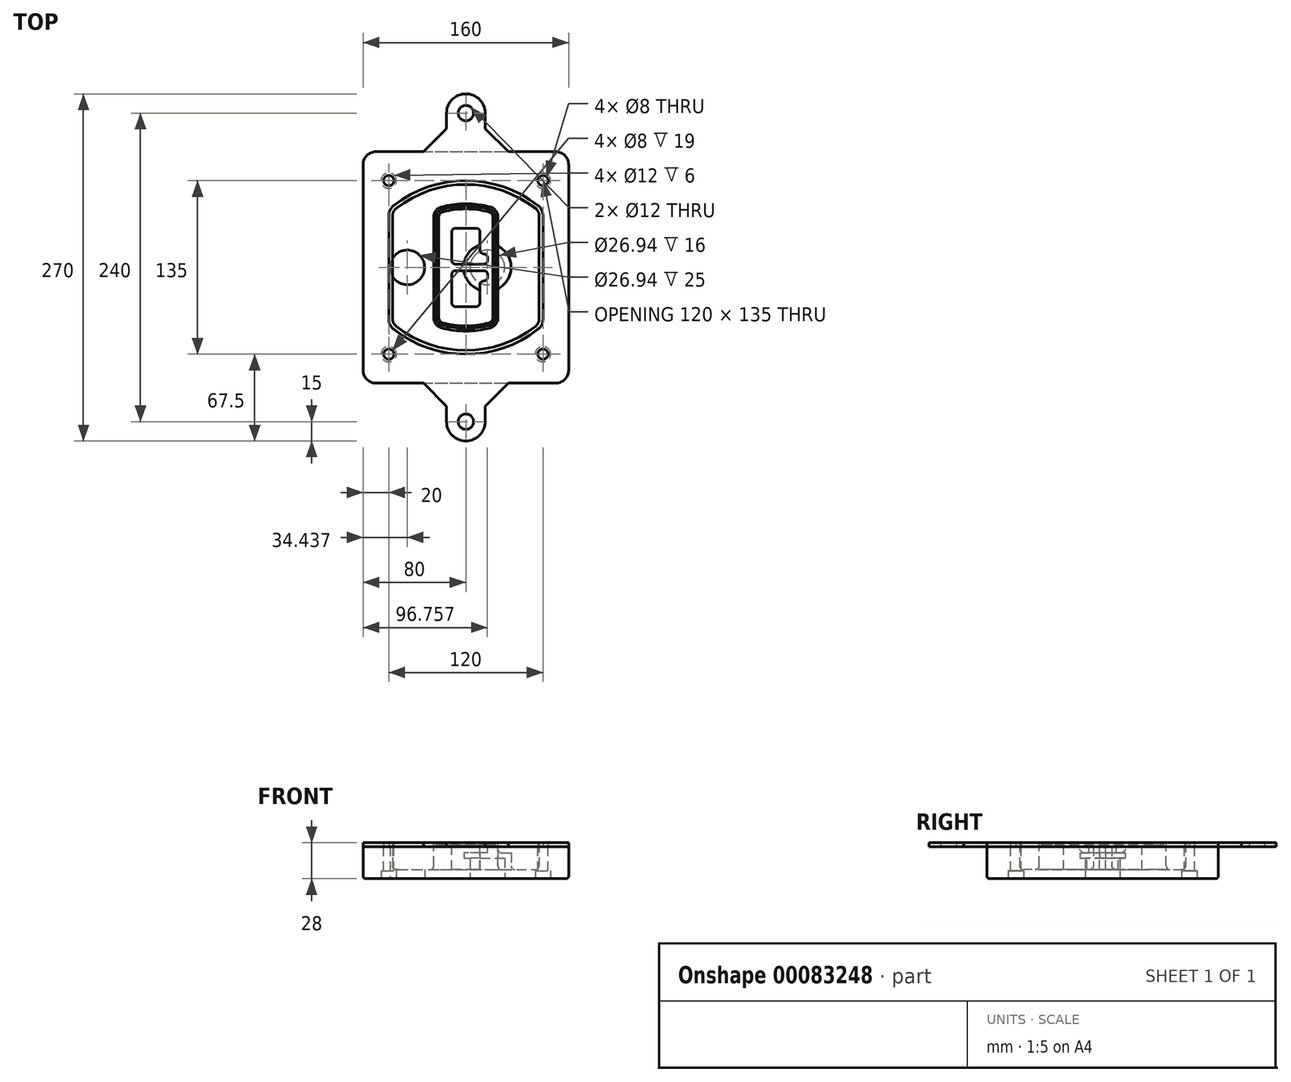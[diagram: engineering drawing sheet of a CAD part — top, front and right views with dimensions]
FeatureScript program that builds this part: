
annotation { "Feature Type Name" : "Feature", "Feature Type Description" : "" }
export const myFeature = defineFeature(function(context is Context, id is Id, definition is map)
    precondition{}
    {
        {
            var Q0;
            Q0=qCreatedBy(makeId("Top.planeOp"),FACE);
            var sketch = newSketch(context, id + "F0", { "sketchPlane" : qUnion([Q0])});
            skPoint(sketch, "E0.rect.middle", {"position": v(0, 0) * mm});
            skLineSegment(sketch, "E1.bottom", {"start": v(-70, -90) * mm, "end": v(70, -90) * mm});
            skLineSegment(sketch, "E1.top", {"start": v(-70, 90) * mm, "end": v(70, 90) * mm});
            skLineSegment(sketch, "E1.left", {"start": v(-80, -80) * mm, "end": v(-80, 80) * mm});
            skLineSegment(sketch, "E1.right", {"start": v(80, -80) * mm, "end": v(80, 80) * mm});
            skLineSegment(sketch, "E2", {"start": v(-80, 90) * mm, "end": v(80, -90) * mm, "construction": true});
            skLineSegment(sketch, "E3", {"start": v(80, 90) * mm, "end": v(-80, -90) * mm, "construction": true});
            skCircle(sketch, "E4", {"center": v(-60, 67.5) * mm, "radius": 4 * mm});
            skCircle(sketch, "E5", {"center": v(60, 67.5) * mm, "radius": 4 * mm});
            skCircle(sketch, "E6", {"center": v(60, -67.5) * mm, "radius": 4 * mm});
            skCircle(sketch, "E7", {"center": v(-60, -67.5) * mm, "radius": 4 * mm});
            skLineSegment(sketch, "E8", {"start": v(-60, 67.5) * mm, "end": v(60, 67.5) * mm, "construction": true});
            skLineSegment(sketch, "E9", {"start": v(60, 67.5) * mm, "end": v(60, -67.5) * mm, "construction": true});
            skLineSegment(sketch, "E10", {"start": v(60, -67.5) * mm, "end": v(-60, -67.5) * mm, "construction": true});
            skLineSegment(sketch, "E11", {"start": v(-60, -67.5) * mm, "end": v(-60, 67.5) * mm, "construction": true});
            skLineSegment(sketch, "E12", {"start": v(-60, 40.3) * mm, "end": v(-60, -40.3) * mm});
            skLineSegment(sketch, "E13", {"start": v(60, 40.3) * mm, "end": v(60, -40.3) * mm});
            skArc(sketch, "E14", {"start": v(56.15, 48.18) * mm, "mid": v(0, 67.5) * mm, "end": v(-56.15, 48.18) * mm});
            skArc(sketch, "E15", {"start": v(-56.15, -48.18) * mm, "mid": v(0, -67.5) * mm, "end": v(56.15, -48.18) * mm});
            skLineSegment(sketch, "E16", {"start": v(-60, 0) * mm, "end": v(60, 0) * mm, "construction": true});
            skPoint(sketch, "E17.visualSharp", {"position": v(-60, -45) * mm});
            skArc(sketch, "E17.filletArc", {"start": v(-60, -40.3) * mm, "mid": v(-58.99, -44.68) * mm, "end": v(-56.15, -48.18) * mm});
            skPoint(sketch, "E18.visualSharp", {"position": v(-60, 45) * mm});
            skArc(sketch, "E18.filletArc", {"start": v(-56.15, 48.18) * mm, "mid": v(-58.99, 44.68) * mm, "end": v(-60, 40.3) * mm});
            skPoint(sketch, "E19.visualSharp", {"position": v(60, 45) * mm});
            skArc(sketch, "E19.filletArc", {"start": v(60, 40.3) * mm, "mid": v(58.99, 44.68) * mm, "end": v(56.15, 48.18) * mm});
            skPoint(sketch, "E20.visualSharp", {"position": v(60, -45) * mm});
            skArc(sketch, "E20.filletArc", {"start": v(56.15, -48.18) * mm, "mid": v(58.99, -44.68) * mm, "end": v(60, -40.3) * mm});
            skPoint(sketch, "E21.visualSharp", {"position": v(-80, 90) * mm});
            skArc(sketch, "E21.filletArc", {"start": v(-70, 90) * mm, "mid": v(-77.07, 87.07) * mm, "end": v(-80, 80) * mm});
            skPoint(sketch, "E22.visualSharp", {"position": v(80, 90) * mm});
            skArc(sketch, "E22.filletArc", {"start": v(80, 80) * mm, "mid": v(77.07, 87.07) * mm, "end": v(70, 90) * mm});
            skPoint(sketch, "E23.visualSharp", {"position": v(80, -90) * mm});
            skArc(sketch, "E23.filletArc", {"start": v(70, -90) * mm, "mid": v(77.07, -87.07) * mm, "end": v(80, -80) * mm});
            skPoint(sketch, "E24.visualSharp", {"position": v(-80, -90) * mm});
            skArc(sketch, "E24.filletArc", {"start": v(-80, -80) * mm, "mid": v(-77.07, -87.07) * mm, "end": v(-70, -90) * mm});
            skArc(sketch, "E25.0", {"start": v(57, 40.3) * mm, "mid": v(56.3, 43.36) * mm, "end": v(54.3, 45.81) * mm});
            skLineSegment(sketch, "E25.1", {"start": v(57, 40.3) * mm, "end": v(57, -40.3) * mm});
            skArc(sketch, "E25.2", {"start": v(54.3, -45.81) * mm, "mid": v(56.3, -43.36) * mm, "end": v(57, -40.3) * mm});
            skArc(sketch, "E25.3", {"start": v(-54.3, -45.81) * mm, "mid": v(0, -64.5) * mm, "end": v(54.3, -45.81) * mm});
            skArc(sketch, "E25.4", {"start": v(-57, -40.3) * mm, "mid": v(-56.3, -43.36) * mm, "end": v(-54.3, -45.81) * mm});
            skArc(sketch, "E25.5", {"start": v(54.3, 45.81) * mm, "mid": v(0, 64.5) * mm, "end": v(-54.3, 45.81) * mm});
            skLineSegment(sketch, "E25.6", {"start": v(-57, 40.3) * mm, "end": v(-57, -40.3) * mm});
            skArc(sketch, "E25.7", {"start": v(-54.3, 45.81) * mm, "mid": v(-56.3, 43.36) * mm, "end": v(-57, 40.3) * mm});
            skArc(sketch, "E26.0", {"start": v(-58.62, 51.33) * mm, "mid": v(-62.58, 46.43) * mm, "end": v(-64, 40.3) * mm});
            skArc(sketch, "E26.1", {"start": v(58.62, 51.33) * mm, "mid": v(0, 71.5) * mm, "end": v(-58.62, 51.33) * mm});
            skArc(sketch, "E26.2", {"start": v(64, 40.3) * mm, "mid": v(62.58, 46.43) * mm, "end": v(58.62, 51.33) * mm});
            skLineSegment(sketch, "E26.3", {"start": v(64, 40.3) * mm, "end": v(64, -40.3) * mm});
            skArc(sketch, "E26.4", {"start": v(58.62, -51.33) * mm, "mid": v(62.58, -46.43) * mm, "end": v(64, -40.3) * mm});
            skLineSegment(sketch, "E26.5", {"start": v(-64, 40.3) * mm, "end": v(-64, -40.3) * mm});
            skArc(sketch, "E26.6", {"start": v(-58.62, -51.33) * mm, "mid": v(0, -71.5) * mm, "end": v(58.62, -51.33) * mm});
            skArc(sketch, "E26.7", {"start": v(-64, -40.3) * mm, "mid": v(-62.58, -46.43) * mm, "end": v(-58.62, -51.33) * mm});
            skSolve(sketch);
        }
        {
            var Q0;
            Q0=makeQuery(id+"F0.imprint","IMPRINT",FACE,{"disambiguationData":[TD([[makeQuery(id+"F0.imprint","IMPRINT",EDGE,{"derivedFrom":sQuery(id+"F0.wireOp",EDGE,"E1.bottom")}),1.0]])]});
            var Q1;
            Q1=makeQuery(id+"F0.imprint","IMPRINT",FACE,{"disambiguationData":[TD([[makeQuery(id+"F0.imprint","IMPRINT",EDGE,{"derivedFrom":sQuery(id+"F0.wireOp",EDGE,"E12")}),1.0]])]});
            var Q2;
            Q2=makeQuery(id+"F0.imprint","IMPRINT",FACE,{"disambiguationData":[TD([[makeQuery(id+"F0.imprint","IMPRINT",EDGE,{"derivedFrom":sQuery(id+"F0.wireOp",EDGE,"E25.0")}),1.0]])]});
            var Q3;
            Q3=makeQuery(id+"F0.imprint","IMPRINT",FACE,{"disambiguationData":[TD([[makeQuery(id+"F0.imprint","IMPRINT",EDGE,{"derivedFrom":sQuery(id+"F0.wireOp",EDGE,"E12")}),-1.0]])]});
            extrude(context, id + "F1", {"entities" : qUnion([Q0, Q1, Q2, Q3]), "oppositeDirection" : true, "depth" : 25 * mm});
        }
        {
            var Q0;
            Q0=makeQuery(id+"F0.imprint","IMPRINT",FACE,{"disambiguationData":[TD([[makeQuery(id+"F0.imprint","IMPRINT",EDGE,{"derivedFrom":sQuery(id+"F0.wireOp",EDGE,"E12")}),1.0]])]});
            extrude(context, id + "F2", {"entities" : qUnion([Q0]), "operationType" : NewBodyOperationType.ADD, "depth" : 3 * mm});
        }
        {
            var Q0;
            Q0=makeQuery(id+"F0.imprint","IMPRINT",FACE,{"disambiguationData":[TD([[makeQuery(id+"F0.imprint","IMPRINT",EDGE,{"derivedFrom":sQuery(id+"F0.wireOp",EDGE,"E25.0")}),1.0]])]});
            extrude(context, id + "F3", {"entities" : qUnion([Q0]), "operationType" : NewBodyOperationType.REMOVE, "oppositeDirection" : true, "depth" : 18 * mm});
        }
        {
            var Q0;
            Q0=makeQuery(id+"F2.opExtrude","CAP_FACE",FACE,{"disambiguationData":[OSD([sQuery(id+"F0.wireOp",EDGE,"E12"),sQuery(id+"F0.wireOp",EDGE,"E13"),sQuery(id+"F0.wireOp",EDGE,"E14"),sQuery(id+"F0.wireOp",EDGE,"E15"),sQuery(id+"F0.wireOp",EDGE,"E17.filletArc"),sQuery(id+"F0.wireOp",EDGE,"E18.filletArc"),sQuery(id+"F0.wireOp",EDGE,"E19.filletArc"),sQuery(id+"F0.wireOp",EDGE,"E20.filletArc"),sQuery(id+"F0.wireOp",EDGE,"E25.0"),sQuery(id+"F0.wireOp",EDGE,"E25.1"),sQuery(id+"F0.wireOp",EDGE,"E25.2"),sQuery(id+"F0.wireOp",EDGE,"E25.3"),sQuery(id+"F0.wireOp",EDGE,"E25.4"),sQuery(id+"F0.wireOp",EDGE,"E25.5"),sQuery(id+"F0.wireOp",EDGE,"E25.6"),sQuery(id+"F0.wireOp",EDGE,"E25.7")])],"isStart":false});
            var sketch = newSketch(context, id + "F4", { "sketchPlane" : qUnion([Q0])});
            skArc(sketch, "E27.0", {"start": v(-19.08, -46.97) * mm, "mid": v(0, -49.5) * mm, "end": v(19.08, -46.97) * mm});
            skArc(sketch, "E28.0", {"start": v(19.08, 46.97) * mm, "mid": v(0, 49.5) * mm, "end": v(-19.08, 46.97) * mm});
            skLineSegment(sketch, "E29", {"start": v(-25, 39.25) * mm, "end": v(-25, -39.25) * mm});
            skLineSegment(sketch, "E30", {"start": v(25, 39.25) * mm, "end": v(25, -39.25) * mm});
            skLineSegment(sketch, "E31", {"start": v(-25, 45.1) * mm, "end": v(25, 45.1) * mm, "construction": true});
            skLineSegment(sketch, "E32", {"start": v(-25, -45.1) * mm, "end": v(25, -45.1) * mm, "construction": true});
            skPoint(sketch, "E33.visualSharp", {"position": v(-25, 45.1) * mm});
            skArc(sketch, "E33.filletArc", {"start": v(-19.08, 46.97) * mm, "mid": v(-23.35, 44.11) * mm, "end": v(-25, 39.25) * mm});
            skPoint(sketch, "E34.visualSharp", {"position": v(25, 45.1) * mm});
            skArc(sketch, "E34.filletArc", {"start": v(25, 39.25) * mm, "mid": v(23.35, 44.11) * mm, "end": v(19.08, 46.97) * mm});
            skPoint(sketch, "E35.visualSharp", {"position": v(25, -45.1) * mm});
            skArc(sketch, "E35.filletArc", {"start": v(19.08, -46.97) * mm, "mid": v(23.35, -44.11) * mm, "end": v(25, -39.25) * mm});
            skPoint(sketch, "E36.visualSharp", {"position": v(-25, -45.1) * mm});
            skArc(sketch, "E36.filletArc", {"start": v(-25, -39.25) * mm, "mid": v(-23.35, -44.11) * mm, "end": v(-19.08, -46.97) * mm});
            skArc(sketch, "E37.0", {"start": v(54.3, 45.81) * mm, "mid": v(0, 64.5) * mm, "end": v(-54.3, 45.81) * mm});
            skArc(sketch, "E37.1", {"start": v(-54.3, 45.81) * mm, "mid": v(-56.3, 43.36) * mm, "end": v(-57, 40.3) * mm});
            skLineSegment(sketch, "E37.2", {"start": v(-57, 40.3) * mm, "end": v(-57, -40.3) * mm});
            skArc(sketch, "E37.3", {"start": v(-57, -40.3) * mm, "mid": v(-56.3, -43.36) * mm, "end": v(-54.3, -45.81) * mm});
            skArc(sketch, "E37.4", {"start": v(-54.3, -45.81) * mm, "mid": v(0, -64.5) * mm, "end": v(54.3, -45.81) * mm});
            skArc(sketch, "E37.5", {"start": v(54.3, -45.81) * mm, "mid": v(56.3, -43.36) * mm, "end": v(57, -40.3) * mm});
            skLineSegment(sketch, "E37.6", {"start": v(57, 40.3) * mm, "end": v(57, -40.3) * mm});
            skArc(sketch, "E37.7", {"start": v(57, 40.3) * mm, "mid": v(56.3, 43.36) * mm, "end": v(54.3, 45.81) * mm});
            skLineSegment(sketch, "E38.0", {"start": v(23, 39.25) * mm, "end": v(23, -39.25) * mm});
            skArc(sketch, "E38.1", {"start": v(18.56, -45.04) * mm, "mid": v(21.76, -42.9) * mm, "end": v(23, -39.25) * mm});
            skArc(sketch, "E38.2", {"start": v(-18.56, -45.04) * mm, "mid": v(0, -47.5) * mm, "end": v(18.56, -45.04) * mm});
            skArc(sketch, "E38.3", {"start": v(-23, -39.25) * mm, "mid": v(-21.76, -42.9) * mm, "end": v(-18.56, -45.04) * mm});
            skLineSegment(sketch, "E38.4", {"start": v(-23, 39.25) * mm, "end": v(-23, -39.25) * mm});
            skArc(sketch, "E38.5", {"start": v(23, 39.25) * mm, "mid": v(21.76, 42.9) * mm, "end": v(18.56, 45.04) * mm});
            skArc(sketch, "E38.6", {"start": v(-18.56, 45.04) * mm, "mid": v(-21.76, 42.9) * mm, "end": v(-23, 39.25) * mm});
            skArc(sketch, "E38.7", {"start": v(18.56, 45.04) * mm, "mid": v(0, 47.5) * mm, "end": v(-18.56, 45.04) * mm});
            skArc(sketch, "E39.0", {"start": v(21, 39.25) * mm, "mid": v(20.18, 41.68) * mm, "end": v(18.04, 43.1) * mm});
            skLineSegment(sketch, "E39.1", {"start": v(21, 39.25) * mm, "end": v(21, -39.25) * mm});
            skArc(sketch, "E39.2", {"start": v(18.04, -43.1) * mm, "mid": v(20.18, -41.68) * mm, "end": v(21, -39.25) * mm});
            skArc(sketch, "E39.3", {"start": v(-18.04, -43.1) * mm, "mid": v(0, -45.5) * mm, "end": v(18.04, -43.1) * mm});
            skArc(sketch, "E39.4", {"start": v(-21, -39.25) * mm, "mid": v(-20.18, -41.68) * mm, "end": v(-18.04, -43.1) * mm});
            skArc(sketch, "E39.5", {"start": v(18.04, 43.1) * mm, "mid": v(0, 45.5) * mm, "end": v(-18.04, 43.1) * mm});
            skLineSegment(sketch, "E39.6", {"start": v(-21, 39.25) * mm, "end": v(-21, -39.25) * mm});
            skArc(sketch, "E39.7", {"start": v(-18.04, 43.1) * mm, "mid": v(-20.18, 41.68) * mm, "end": v(-21, 39.25) * mm});
            skLineSegment(sketch, "E40", {"start": v(-25, 0) * mm, "end": v(25, 0) * mm, "construction": true});
            skLineSegment(sketch, "E41", {"start": v(-11, 5.5) * mm, "end": v(-11, 27.5) * mm});
            skLineSegment(sketch, "E42", {"start": v(-8, 30.5) * mm, "end": v(8, 30.5) * mm});
            skLineSegment(sketch, "E43", {"start": v(11, 27.5) * mm, "end": v(11, 13.5) * mm});
            skLineSegment(sketch, "E44", {"start": v(14, 10.5) * mm, "end": v(14, 10.5) * mm});
            skLineSegment(sketch, "E45", {"start": v(17, 7.5) * mm, "end": v(17, 5.5) * mm});
            skLineSegment(sketch, "E46", {"start": v(14, 2.5) * mm, "end": v(-8, 2.5) * mm});
            skPoint(sketch, "E47.visualSharp", {"position": v(-11, 30.5) * mm});
            skArc(sketch, "E47.filletArc", {"start": v(-8, 30.5) * mm, "mid": v(-10.12, 29.62) * mm, "end": v(-11, 27.5) * mm});
            skPoint(sketch, "E48.visualSharp", {"position": v(11, 30.5) * mm});
            skArc(sketch, "E48.filletArc", {"start": v(11, 27.5) * mm, "mid": v(10.12, 29.62) * mm, "end": v(8, 30.5) * mm});
            skPoint(sketch, "E49.visualSharp", {"position": v(11, 10.5) * mm});
            skArc(sketch, "E49.filletArc", {"start": v(11, 13.5) * mm, "mid": v(11.88, 11.38) * mm, "end": v(14, 10.5) * mm});
            skPoint(sketch, "E50.visualSharp", {"position": v(17, 10.5) * mm});
            skArc(sketch, "E50.filletArc", {"start": v(17, 7.5) * mm, "mid": v(16.12, 9.62) * mm, "end": v(14, 10.5) * mm});
            skPoint(sketch, "E51.visualSharp", {"position": v(17, 2.5) * mm});
            skArc(sketch, "E51.filletArc", {"start": v(14, 2.5) * mm, "mid": v(16.12, 3.38) * mm, "end": v(17, 5.5) * mm});
            skPoint(sketch, "E52.visualSharp", {"position": v(-11, 2.5) * mm});
            skArc(sketch, "E52.filletArc", {"start": v(-11, 5.5) * mm, "mid": v(-10.12, 3.38) * mm, "end": v(-8, 2.5) * mm});
            skLineSegment(sketch, "E53.0.MirrorCS", {"start": v(14, -2.5) * mm, "end": v(-8, -2.5) * mm});
            skArc(sketch, "E54.0.MirrorCS", {"start": v(-11, -5.5) * mm, "mid": v(-10.12, -3.38) * mm, "end": v(-8, -2.5) * mm});
            skLineSegment(sketch, "E55.0.MirrorCS", {"start": v(-11, -5.5) * mm, "end": v(-11, -27.5) * mm});
            skArc(sketch, "E56.0.MirrorCS", {"start": v(-8, -30.5) * mm, "mid": v(-10.12, -29.62) * mm, "end": v(-11, -27.5) * mm});
            skLineSegment(sketch, "E57.0.MirrorCS", {"start": v(-8, -30.5) * mm, "end": v(8, -30.5) * mm});
            skArc(sketch, "E58.0.MirrorCS", {"start": v(11, -27.5) * mm, "mid": v(10.12, -29.62) * mm, "end": v(8, -30.5) * mm});
            skLineSegment(sketch, "E59.0.MirrorCS", {"start": v(11, -27.5) * mm, "end": v(11, -13.5) * mm});
            skArc(sketch, "E60.0.MirrorCS", {"start": v(11, -13.5) * mm, "mid": v(11.88, -11.38) * mm, "end": v(14, -10.5) * mm});
            skArc(sketch, "E61.0.MirrorCS", {"start": v(17, -7.5) * mm, "mid": v(16.12, -9.62) * mm, "end": v(14, -10.5) * mm});
            skLineSegment(sketch, "E62.0.MirrorCS", {"start": v(17, -7.5) * mm, "end": v(17, -5.5) * mm});
            skArc(sketch, "E63.0.MirrorCS", {"start": v(14, -2.5) * mm, "mid": v(16.12, -3.38) * mm, "end": v(17, -5.5) * mm});
            skSolve(sketch);
        }
        {
            var Q0;
            Q0=makeQuery(id+"F4.imprint","IMPRINT",FACE,{"disambiguationData":[TD([[makeQuery(id+"F4.imprint","IMPRINT",EDGE,{"derivedFrom":sQuery(id+"F4.wireOp",EDGE,"E27.0")}),1.0]])]});
            var Q1;
            Q1=makeQuery(id+"F4.imprint","IMPRINT",FACE,{"disambiguationData":[TD([[makeQuery(id+"F4.imprint","IMPRINT",EDGE,{"derivedFrom":sQuery(id+"F4.wireOp",EDGE,"E38.0")}),-1.0]])]});
            var Q2;
            Q2=makeQuery(id+"F4.imprint","IMPRINT",FACE,{"disambiguationData":[TD([[makeQuery(id+"F4.imprint","IMPRINT",EDGE,{"derivedFrom":sQuery(id+"F4.wireOp",EDGE,"E39.0")}),1.0]])]});
            extrude(context, id + "F5", {"entities" : qUnion([Q0, Q1, Q2]), "operationType" : NewBodyOperationType.ADD, "endBound" : BoundingType.UP_TO_NEXT, "oppositeDirection" : true, "depth" : 25 * mm});
        }
        {
            var Q0;
            Q0=makeQuery(id+"F4.imprint","IMPRINT",FACE,{"disambiguationData":[TD([[makeQuery(id+"F4.imprint","IMPRINT",EDGE,{"derivedFrom":sQuery(id+"F4.wireOp",EDGE,"E38.0")}),-1.0]])]});
            extrude(context, id + "F6", {"entities" : qUnion([Q0]), "operationType" : NewBodyOperationType.REMOVE, "oppositeDirection" : true, "depth" : 2 * mm});
        }
        {
            var Q0;
            Q0=makeQuery(id+"F1.opExtrude","CAP_FACE",FACE,{"disambiguationData":[OSD([sQuery(id+"F0.wireOp",EDGE,"E1.bottom"),sQuery(id+"F0.wireOp",EDGE,"E1.top"),sQuery(id+"F0.wireOp",EDGE,"E1.left"),sQuery(id+"F0.wireOp",EDGE,"E1.right"),sQuery(id+"F0.wireOp",EDGE,"E4"),sQuery(id+"F0.wireOp",EDGE,"E5"),sQuery(id+"F0.wireOp",EDGE,"E6"),sQuery(id+"F0.wireOp",EDGE,"E7"),sQuery(id+"F0.wireOp",EDGE,"E21.filletArc"),sQuery(id+"F0.wireOp",EDGE,"E22.filletArc"),sQuery(id+"F0.wireOp",EDGE,"E23.filletArc"),sQuery(id+"F0.wireOp",EDGE,"E24.filletArc")])],"isStart":false});
            var sketch = newSketch(context, id + "F7", { "sketchPlane" : qUnion([Q0])});
            skCircle(sketch, "E64", {"center": v(16.76, 0) * mm, "radius": 13.47 * mm});
            skCircle(sketch, "E65", {"center": v(-45.56, 0) * mm, "radius": 13.47 * mm});
            skLineSegment(sketch, "E66", {"start": v(80, 0) * mm, "end": v(-80, 0) * mm});
            skCircle(sketch, "E67", {"center": v(16.76, 0) * mm, "radius": 18.47 * mm});
            skCircle(sketch, "E68", {"center": v(60, -67.5) * mm, "radius": 6 * mm});
            skCircle(sketch, "E69", {"center": v(-60, -67.5) * mm, "radius": 6 * mm});
            skCircle(sketch, "E70", {"center": v(-60, 67.5) * mm, "radius": 6 * mm});
            skCircle(sketch, "E71", {"center": v(60, 67.5) * mm, "radius": 6 * mm});
            skSolve(sketch);
        }
        {
            var Q0;
            {var subQ1=sQuery(id+"F7.wireOp",EDGE,"E66");var subQ4=sQuery(id+"F7.wireOp",EDGE,"E64");var subQ6=makeQuery(id+"F7.imprint","INTERSECT",VERTEX,{"disambiguationData":[OD(0.0)],"derivedFrom":[subQ4,subQ1]});Q0=makeQuery(id+"F7.imprint","IMPRINT",FACE,{"disambiguationData":[TD([[makeQuery(id+"F7.imprint","IMPRINT",EDGE,{"disambiguationData":[TD([[subQ6,-1.0]])],"derivedFrom":subQ4}),-1.0]])]});}
            var Q1;
            {var subQ0=sQuery(id+"F7.wireOp",EDGE,"E66");var subQ1=sQuery(id+"F7.wireOp",EDGE,"E64");var subQ3=makeQuery(id+"F7.imprint","INTERSECT",VERTEX,{"disambiguationData":[OD(0.0)],"derivedFrom":[subQ1,subQ0]});Q1=makeQuery(id+"F7.imprint","IMPRINT",FACE,{"disambiguationData":[TD([[makeQuery(id+"F7.imprint","IMPRINT",EDGE,{"disambiguationData":[TD([[subQ3,-1.0]])],"derivedFrom":subQ1}),1.0]])]});}
            var Q2;
            {var subQ0=sQuery(id+"F7.wireOp",EDGE,"E66");var subQ1=sQuery(id+"F7.wireOp",EDGE,"E64");var subQ3=makeQuery(id+"F7.imprint","INTERSECT",VERTEX,{"disambiguationData":[OD(0.0)],"derivedFrom":[subQ1,subQ0]});Q2=makeQuery(id+"F7.imprint","IMPRINT",FACE,{"disambiguationData":[TD([[makeQuery(id+"F7.imprint","IMPRINT",EDGE,{"disambiguationData":[TD([[subQ3,1.0]])],"derivedFrom":subQ1}),1.0]])]});}
            var Q3;
            {var subQ1=sQuery(id+"F7.wireOp",EDGE,"E66");var subQ4=sQuery(id+"F7.wireOp",EDGE,"E64");var subQ6=makeQuery(id+"F7.imprint","INTERSECT",VERTEX,{"disambiguationData":[OD(0.0)],"derivedFrom":[subQ4,subQ1]});Q3=makeQuery(id+"F7.imprint","IMPRINT",FACE,{"disambiguationData":[TD([[makeQuery(id+"F7.imprint","IMPRINT",EDGE,{"disambiguationData":[TD([[subQ6,1.0]])],"derivedFrom":subQ4}),-1.0]])]});}
            extrude(context, id + "F8", {"entities" : qUnion([Q0, Q1, Q2, Q3]), "operationType" : NewBodyOperationType.ADD, "oppositeDirection" : true, "depth" : 20 * mm});
        }
        {
            var Q0;
            {var subQ0=sQuery(id+"F7.wireOp",EDGE,"E66");var subQ1=sQuery(id+"F7.wireOp",EDGE,"E64");var subQ3=makeQuery(id+"F7.imprint","INTERSECT",VERTEX,{"disambiguationData":[OD(0.0)],"derivedFrom":[subQ1,subQ0]});Q0=makeQuery(id+"F7.imprint","IMPRINT",FACE,{"disambiguationData":[TD([[makeQuery(id+"F7.imprint","IMPRINT",EDGE,{"disambiguationData":[TD([[subQ3,-1.0]])],"derivedFrom":subQ1}),1.0]])]});}
            var Q1;
            {var subQ0=sQuery(id+"F7.wireOp",EDGE,"E66");var subQ1=sQuery(id+"F7.wireOp",EDGE,"E64");var subQ3=makeQuery(id+"F7.imprint","INTERSECT",VERTEX,{"disambiguationData":[OD(0.0)],"derivedFrom":[subQ1,subQ0]});Q1=makeQuery(id+"F7.imprint","IMPRINT",FACE,{"disambiguationData":[TD([[makeQuery(id+"F7.imprint","IMPRINT",EDGE,{"disambiguationData":[TD([[subQ3,1.0]])],"derivedFrom":subQ1}),1.0]])]});}
            extrude(context, id + "F9", {"entities" : qUnion([Q0, Q1]), "operationType" : NewBodyOperationType.REMOVE, "oppositeDirection" : true, "depth" : 16 * mm});
        }
        {
            var Q0;
            {var subQ0=sQuery(id+"F7.wireOp",EDGE,"E66");var subQ1=sQuery(id+"F7.wireOp",EDGE,"E65");var subQ3=makeQuery(id+"F7.imprint","INTERSECT",VERTEX,{"disambiguationData":[OD(0.0)],"derivedFrom":[subQ1,subQ0]});Q0=makeQuery(id+"F7.imprint","IMPRINT",FACE,{"disambiguationData":[TD([[makeQuery(id+"F7.imprint","IMPRINT",EDGE,{"disambiguationData":[TD([[subQ3,-1.0]])],"derivedFrom":subQ1}),1.0]])]});}
            var Q1;
            {var subQ0=sQuery(id+"F7.wireOp",EDGE,"E66");var subQ1=sQuery(id+"F7.wireOp",EDGE,"E65");var subQ3=makeQuery(id+"F7.imprint","INTERSECT",VERTEX,{"disambiguationData":[OD(0.0)],"derivedFrom":[subQ1,subQ0]});Q1=makeQuery(id+"F7.imprint","IMPRINT",FACE,{"disambiguationData":[TD([[makeQuery(id+"F7.imprint","IMPRINT",EDGE,{"disambiguationData":[TD([[subQ3,1.0]])],"derivedFrom":subQ1}),1.0]])]});}
            extrude(context, id + "F10", {"entities" : qUnion([Q0, Q1]), "operationType" : NewBodyOperationType.REMOVE, "oppositeDirection" : true, "depth" : 25 * mm});
        }
        {
            var Q0;
            Q0=makeQuery(id+"F7.imprint","IMPRINT",FACE,{"disambiguationData":[TD([[makeQuery(id+"F7.imprint","IMPRINT",EDGE,{"derivedFrom":sQuery(id+"F7.wireOp",EDGE,"E68")}),1.0]])]});
            var Q1;
            Q1=makeQuery(id+"F7.imprint","IMPRINT",FACE,{"disambiguationData":[TD([[makeQuery(id+"F7.imprint","IMPRINT",EDGE,{"derivedFrom":makeQuery(id+"F1.opExtrude","CAP_EDGE",EDGE,{"disambiguationData":[OSD([sQuery(id+"F0.wireOp",EDGE,"E5")])],"isStart":false})}),-1.0]])]});
            var Q2;
            Q2=makeQuery(id+"F7.imprint","IMPRINT",FACE,{"disambiguationData":[TD([[makeQuery(id+"F7.imprint","IMPRINT",EDGE,{"derivedFrom":sQuery(id+"F7.wireOp",EDGE,"E69")}),1.0]])]});
            var Q3;
            Q3=makeQuery(id+"F7.imprint","IMPRINT",FACE,{"disambiguationData":[TD([[makeQuery(id+"F7.imprint","IMPRINT",EDGE,{"derivedFrom":makeQuery(id+"F1.opExtrude","CAP_EDGE",EDGE,{"disambiguationData":[OSD([sQuery(id+"F0.wireOp",EDGE,"E4")])],"isStart":false})}),-1.0]])]});
            var Q4;
            Q4=makeQuery(id+"F7.imprint","IMPRINT",FACE,{"disambiguationData":[TD([[makeQuery(id+"F7.imprint","IMPRINT",EDGE,{"derivedFrom":sQuery(id+"F7.wireOp",EDGE,"E70")}),1.0]])]});
            var Q5;
            Q5=makeQuery(id+"F7.imprint","IMPRINT",FACE,{"disambiguationData":[TD([[makeQuery(id+"F7.imprint","IMPRINT",EDGE,{"derivedFrom":makeQuery(id+"F1.opExtrude","CAP_EDGE",EDGE,{"disambiguationData":[OSD([sQuery(id+"F0.wireOp",EDGE,"E7")])],"isStart":false})}),-1.0]])]});
            var Q6;
            Q6=makeQuery(id+"F7.imprint","IMPRINT",FACE,{"disambiguationData":[TD([[makeQuery(id+"F7.imprint","IMPRINT",EDGE,{"derivedFrom":sQuery(id+"F7.wireOp",EDGE,"E71")}),1.0]])]});
            var Q7;
            Q7=makeQuery(id+"F7.imprint","IMPRINT",FACE,{"disambiguationData":[TD([[makeQuery(id+"F7.imprint","IMPRINT",EDGE,{"derivedFrom":makeQuery(id+"F1.opExtrude","CAP_EDGE",EDGE,{"disambiguationData":[OSD([sQuery(id+"F0.wireOp",EDGE,"E6")])],"isStart":false})}),-1.0]])]});
            extrude(context, id + "F11", {"entities" : qUnion([Q0, Q1, Q2, Q3, Q4, Q5, Q6, Q7]), "operationType" : NewBodyOperationType.REMOVE, "oppositeDirection" : true, "depth" : 6 * mm});
        }
        {
            var Q0;
            Q0=makeQuery(id+"F9.boolean.opBoolean","COPY",FACE,{"derivedFrom":makeQuery(id+"F9.opExtrude","CAP_FACE",FACE,{"disambiguationData":[OSD([sQuery(id+"F7.wireOp",EDGE,"E64")])],"isStart":false})});
            var sketch = newSketch(context, id + "F12", { "sketchPlane" : qUnion([Q0])});
            skArc(sketch, "E72.0", {"start": v(11, 17.55) * mm, "mid": v(2.57, 11.82) * mm, "end": v(-1.54, 2.5) * mm});
            skArc(sketch, "E72.1", {"start": v(-1.54, -2.5) * mm, "mid": v(2.57, -11.82) * mm, "end": v(11, -17.55) * mm});
            skLineSegment(sketch, "E73", {"start": v(-1.54, -2.5) * mm, "end": v(14, -2.5) * mm});
            skLineSegment(sketch, "E74.0", {"start": v(14, 2.5) * mm, "end": v(-1.54, 2.5) * mm});
            skArc(sketch, "E74.1", {"start": v(14, 2.5) * mm, "mid": v(16.12, 3.38) * mm, "end": v(17, 5.5) * mm});
            skLineSegment(sketch, "E74.2", {"start": v(17, 7.5) * mm, "end": v(17, 5.5) * mm});
            skArc(sketch, "E74.3", {"start": v(17, 7.5) * mm, "mid": v(16.12, 9.62) * mm, "end": v(14, 10.5) * mm});
            skArc(sketch, "E74.4", {"start": v(11, 13.5) * mm, "mid": v(11.88, 11.38) * mm, "end": v(14, 10.5) * mm});
            skLineSegment(sketch, "E74.5", {"start": v(11, 17.55) * mm, "end": v(11, 13.5) * mm});
            skLineSegment(sketch, "E74.7", {"start": v(14, -2.5) * mm, "end": v(-1.54, -2.5) * mm});
            skArc(sketch, "E74.8", {"start": v(14, -2.5) * mm, "mid": v(16.12, -3.38) * mm, "end": v(17, -5.5) * mm});
            skLineSegment(sketch, "E74.9", {"start": v(17, -7.5) * mm, "end": v(17, -5.5) * mm});
            skArc(sketch, "E74.10", {"start": v(17, -7.5) * mm, "mid": v(16.12, -9.62) * mm, "end": v(14, -10.5) * mm});
            skArc(sketch, "E74.11", {"start": v(11, -13.5) * mm, "mid": v(11.88, -11.38) * mm, "end": v(14, -10.5) * mm});
            skLineSegment(sketch, "E74.12", {"start": v(11, -17.55) * mm, "end": v(11, -13.5) * mm});
            skPoint(sketch, "E75.orphan", {"position": v(11, -27.5) * mm});
            skPoint(sketch, "E76.orphan", {"position": v(-8, -2.5) * mm});
            skPoint(sketch, "E77.orphan", {"position": v(-8, 2.5) * mm});
            skPoint(sketch, "E78.orphan", {"position": v(11, 27.5) * mm});
            skSolve(sketch);
        }
        {
            var Q0;
            {var subQ7=sQuery(id+"F12.wireOp",EDGE,"E72.0");var subQ14=sQuery(id+"F12.wireOp",EDGE,"E72.1");var subQ16=sQuery(id+"F12.wireOp",EDGE,"E74.1");var subQ18=sQuery(id+"F12.wireOp",EDGE,"E74.8");Q0=qUnion([makeQuery(id+"F12.imprint","IMPRINT",FACE,{"disambiguationData":[TD([[makeQuery(id+"F12.imprint","IMPRINT",EDGE,{"derivedFrom":subQ7}),1.0]])]}),makeQuery(id+"F12.imprint","IMPRINT",FACE,{"disambiguationData":[TD([[makeQuery(id+"F12.imprint","IMPRINT",EDGE,{"derivedFrom":subQ14}),1.0]])]}),makeQuery(id+"F12.imprint","IMPRINT",FACE,{"disambiguationData":[TD([[makeQuery(id+"F12.imprint","IMPRINT",EDGE,{"derivedFrom":subQ16}),1.0]])]}),makeQuery(id+"F12.imprint","IMPRINT",FACE,{"disambiguationData":[TD([[makeQuery(id+"F12.imprint","IMPRINT",EDGE,{"derivedFrom":subQ18}),-1.0]])]})]);}
            var Q1;
            Q1=makeQuery(id+"F5.boolean.opBoolean","SPLIT",FACE,{"disambiguationData":[TD([makeQuery(id+"F5.opExtrude","SWEPT_FACE",FACE,{"disambiguationData":[OSD([sQuery(id+"F4.wireOp",EDGE,"E41")])]})])],"derivedFrom":makeQuery(id+"F3.boolean.opBoolean","COPY",FACE,{"derivedFrom":makeQuery(id+"F3.opExtrude","CAP_FACE",FACE,{"disambiguationData":[OSD([sQuery(id+"F0.wireOp",EDGE,"E25.0"),sQuery(id+"F0.wireOp",EDGE,"E25.1"),sQuery(id+"F0.wireOp",EDGE,"E25.2"),sQuery(id+"F0.wireOp",EDGE,"E25.3"),sQuery(id+"F0.wireOp",EDGE,"E25.4"),sQuery(id+"F0.wireOp",EDGE,"E25.5"),sQuery(id+"F0.wireOp",EDGE,"E25.6"),sQuery(id+"F0.wireOp",EDGE,"E25.7")])],"isStart":false})})});
            extrude(context, id + "F13", {"entities" : qUnion([Q0]), "operationType" : NewBodyOperationType.REMOVE, "endBound" : BoundingType.UP_TO_SURFACE, "endBoundEntityFace" : qUnion([Q1]), "depth" : 25 * mm});
        }
        {
            var Q0;
            Q0=makeQuery(id+"F3.boolean.opBoolean","COPY",EDGE,{"derivedFrom":makeQuery(id+"F3.opExtrude","CAP_EDGE",EDGE,{"disambiguationData":[OSD([sQuery(id+"F0.wireOp",EDGE,"E25.6")])],"isStart":false})});
            var Q1;
            Q1=makeQuery(id+"F8.boolean.opBoolean","INTERSECT",EDGE,{"derivedFrom":[makeQuery(id+"F5.opExtrude","SWEPT_FACE",FACE,{"disambiguationData":[OSD([sQuery(id+"F4.wireOp",EDGE,"E30")])]}),makeQuery(id+"F8.opExtrude","CAP_FACE",FACE,{"disambiguationData":[OSD([sQuery(id+"F7.wireOp",EDGE,"E67")])],"isStart":false})]});
            var Q2;
            Q2=makeQuery(id+"F8.boolean.opBoolean","INTERSECT",EDGE,{"disambiguationData":[OD(1.0)],"derivedFrom":[makeQuery(id+"F5.opExtrude","SWEPT_FACE",FACE,{"disambiguationData":[OSD([sQuery(id+"F4.wireOp",EDGE,"E30")])]}),makeQuery(id+"F8.opExtrude","SWEPT_FACE",FACE,{"disambiguationData":[OSD([sQuery(id+"F7.wireOp",EDGE,"E67")])]})]});
            var Q3;
            {var subQ0=sQuery(id+"F4.wireOp",EDGE,"E30");Q3=makeQuery(id+"F8.boolean.opBoolean","SPLIT",EDGE,{"disambiguationData":[TD([makeQuery(id+"F5.opExtrude","SWEPT_FACE",FACE,{"disambiguationData":[OSD([sQuery(id+"F4.wireOp",EDGE,"E35.filletArc")])]})])],"derivedFrom":makeQuery(id+"F5.opExtrude","CAP_EDGE",EDGE,{"disambiguationData":[OSD([subQ0])],"isStart":false})});}
            var Q4;
            {var subQ0=sQuery(id+"F0.wireOp",EDGE,"E25.7");var subQ1=sQuery(id+"F0.wireOp",EDGE,"E25.1");var subQ2=sQuery(id+"F0.wireOp",EDGE,"E25.6");var subQ3=sQuery(id+"F0.wireOp",EDGE,"E25.5");var subQ4=sQuery(id+"F0.wireOp",EDGE,"E25.4");var subQ5=sQuery(id+"F0.wireOp",EDGE,"E25.0");var subQ6=sQuery(id+"F0.wireOp",EDGE,"E25.2");var subQ7=sQuery(id+"F0.wireOp",EDGE,"E25.3");Q4=makeQuery(id+"F8.boolean.opBoolean","INTERSECT",EDGE,{"derivedFrom":[makeQuery(id+"F5.boolean.opBoolean","SPLIT",FACE,{"disambiguationData":[TD([makeQuery(id+"F2.opExtrude","SWEPT_FACE",FACE,{"disambiguationData":[OSD([subQ5])]})])],"derivedFrom":makeQuery(id+"F3.boolean.opBoolean","COPY",FACE,{"derivedFrom":makeQuery(id+"F3.opExtrude","CAP_FACE",FACE,{"disambiguationData":[OSD([subQ5,subQ1,subQ6,subQ7,subQ4,subQ3,subQ2,subQ0])],"isStart":false})})}),makeQuery(id+"F8.opExtrude","SWEPT_FACE",FACE,{"disambiguationData":[OSD([sQuery(id+"F7.wireOp",EDGE,"E67")])]})]});}
            var Q5;
            Q5=makeQuery(id+"F8.boolean.opBoolean","INTERSECT",EDGE,{"disambiguationData":[OD(0.0)],"derivedFrom":[makeQuery(id+"F5.opExtrude","SWEPT_FACE",FACE,{"disambiguationData":[OSD([sQuery(id+"F4.wireOp",EDGE,"E30")])]}),makeQuery(id+"F8.opExtrude","SWEPT_FACE",FACE,{"disambiguationData":[OSD([sQuery(id+"F7.wireOp",EDGE,"E67")])]})]});
            fillet(context, id + "F14", {"entities" : qUnion([Q0, Q1, Q2, Q3, Q4, Q5]), "radius" : 3 * mm, "tangentPropagation" : true, "allowEdgeOverflow" : false});
        }
        {
            var Q0;
            Q0=makeQuery(id+"F1.opExtrude","CAP_EDGE",EDGE,{"disambiguationData":[OSD([sQuery(id+"F0.wireOp",EDGE,"E1.bottom")])],"isStart":false});
            fillet(context, id + "F15", {"entities" : qUnion([Q0]), "radius" : 2 * mm, "tangentPropagation" : true, "allowEdgeOverflow" : false});
        }
        {
            var Q0;
            {var subQ0=sQuery(id+"F0.wireOp",EDGE,"E22.filletArc");var subQ1=sQuery(id+"F0.wireOp",EDGE,"E7");var subQ2=sQuery(id+"F0.wireOp",EDGE,"E6");var subQ3=sQuery(id+"F0.wireOp",EDGE,"E5");var subQ4=sQuery(id+"F0.wireOp",EDGE,"E4");var subQ5=sQuery(id+"F0.wireOp",EDGE,"E1.bottom");var subQ6=sQuery(id+"F0.wireOp",EDGE,"E21.filletArc");var subQ7=sQuery(id+"F0.wireOp",EDGE,"E1.top");var subQ8=sQuery(id+"F0.wireOp",EDGE,"E1.left");var subQ9=sQuery(id+"F0.wireOp",EDGE,"E1.right");var subQ10=sQuery(id+"F0.wireOp",EDGE,"E23.filletArc");var subQ11=sQuery(id+"F0.wireOp",EDGE,"E24.filletArc");Q0=makeQuery(id+"F2.boolean.opBoolean","SPLIT",FACE,{"disambiguationData":[TD([makeQuery(id+"F1.opExtrude","SWEPT_FACE",FACE,{"disambiguationData":[OSD([subQ5])]})])],"derivedFrom":makeQuery(id+"F1.opExtrude","CAP_FACE",FACE,{"disambiguationData":[OSD([subQ5,subQ7,subQ8,subQ9,subQ4,subQ3,subQ2,subQ1,subQ6,subQ0,subQ10,subQ11])],"isStart":true})});}
            var sketch = newSketch(context, id + "F16", { "sketchPlane" : qUnion([Q0])});
            skArc(sketch, "E79.0.0", {"start": v(-80, -80) * mm, "mid": v(-77.07, -87.07) * mm, "end": v(-70, -90) * mm});
            skLineSegment(sketch, "E79.0.1", {"start": v(-70, -90) * mm, "end": v(70, -90) * mm});
            skArc(sketch, "E79.0.2", {"start": v(70, -90) * mm, "mid": v(77.07, -87.07) * mm, "end": v(80, -80) * mm});
            skLineSegment(sketch, "E79.0.3", {"start": v(80, -80) * mm, "end": v(80, 80) * mm});
            skArc(sketch, "E79.0.4", {"start": v(80, 80) * mm, "mid": v(77.07, 87.07) * mm, "end": v(70, 90) * mm});
            skLineSegment(sketch, "E79.0.5", {"start": v(70, 90) * mm, "end": v(-70, 90) * mm});
            skArc(sketch, "E79.0.6", {"start": v(-70, 90) * mm, "mid": v(-77.07, 87.07) * mm, "end": v(-80, 80) * mm});
            skLineSegment(sketch, "E79.0.7", {"start": v(-80, 80) * mm, "end": v(-80, -80) * mm});
            skLineSegment(sketch, "E80.0", {"start": v(-60, 40.3) * mm, "end": v(-60, -40.3) * mm});
            skArc(sketch, "E81.0", {"start": v(-56.15, 48.18) * mm, "mid": v(-58.99, 44.68) * mm, "end": v(-60, 40.3) * mm});
            skArc(sketch, "E82.0", {"start": v(56.15, 48.18) * mm, "mid": v(0, 67.5) * mm, "end": v(-56.15, 48.18) * mm});
            skArc(sketch, "E83.0", {"start": v(60, 40.3) * mm, "mid": v(58.99, 44.68) * mm, "end": v(56.15, 48.18) * mm});
            skLineSegment(sketch, "E84.0", {"start": v(60, 40.3) * mm, "end": v(60, -40.3) * mm});
            skArc(sketch, "E85.0", {"start": v(56.15, -48.18) * mm, "mid": v(58.99, -44.68) * mm, "end": v(60, -40.3) * mm});
            skArc(sketch, "E86.0", {"start": v(-56.15, -48.18) * mm, "mid": v(0, -67.5) * mm, "end": v(56.15, -48.18) * mm});
            skArc(sketch, "E87.0", {"start": v(-60, -40.3) * mm, "mid": v(-58.99, -44.68) * mm, "end": v(-56.15, -48.18) * mm});
            skLineSegment(sketch, "E88", {"start": v(0, 90) * mm, "end": v(0, -90) * mm, "construction": true});
            skLineSegment(sketch, "E89", {"start": v(-80, 0) * mm, "end": v(80, 0) * mm, "construction": true});
            skLineSegment(sketch, "E90", {"start": v(-33, 90) * mm, "end": v(-15, 108) * mm});
            skLineSegment(sketch, "E91", {"start": v(-15, 108) * mm, "end": v(-15, 120) * mm});
            skLineSegment(sketch, "E92", {"start": v(15, 120) * mm, "end": v(15, 108) * mm});
            skLineSegment(sketch, "E93", {"start": v(15, 108) * mm, "end": v(33, 90) * mm});
            skArc(sketch, "E94", {"start": v(15, 120) * mm, "mid": v(0, 135) * mm, "end": v(-15, 120) * mm});
            skLineSegment(sketch, "E95", {"start": v(0, 120) * mm, "end": v(0, 90) * mm, "construction": true});
            skCircle(sketch, "E96", {"center": v(0, 120) * mm, "radius": 6 * mm});
            skLineSegment(sketch, "E97.MirrorCS", {"start": v(-33, -90) * mm, "end": v(-15, -108) * mm});
            skLineSegment(sketch, "E98.MirrorCS", {"start": v(-15, -108) * mm, "end": v(-15, -120) * mm});
            skArc(sketch, "E99.MirrorCS", {"start": v(15, -120) * mm, "mid": v(0, -135) * mm, "end": v(-15, -120) * mm});
            skCircle(sketch, "E100.MirrorC", {"center": v(0, -120) * mm, "radius": 6 * mm});
            skLineSegment(sketch, "E101.MirrorCS", {"start": v(15, -120) * mm, "end": v(15, -108) * mm});
            skLineSegment(sketch, "E102.MirrorCS", {"start": v(15, -108) * mm, "end": v(33, -90) * mm});
            skLineSegment(sketch, "E103.MirrorCS", {"start": v(0, -120) * mm, "end": v(0, -90) * mm, "construction": true});
            skCircle(sketch, "E104.0", {"center": v(-60, 67.5) * mm, "radius": 4 * mm});
            skCircle(sketch, "E105.0", {"center": v(60, -67.5) * mm, "radius": 4 * mm});
            skCircle(sketch, "E106.0", {"center": v(-60, -67.5) * mm, "radius": 4 * mm});
            skCircle(sketch, "E107.0", {"center": v(60, 67.5) * mm, "radius": 4 * mm});
            skSolve(sketch);
        }
        {
            var Q0;
            {var subQ8=sQuery(id+"F16.wireOp",EDGE,"E79.0.0");Q0=makeQuery(id+"F16.imprint","IMPRINT",FACE,{"disambiguationData":[TD([[makeQuery(id+"F16.imprint","IMPRINT",EDGE,{"derivedFrom":subQ8}),1.0]])]});}
            var Q1;
            {var subQ8=sQuery(id+"F16.wireOp",EDGE,"E79.0.0");Q1=makeQuery(id+"F16.imprint","IMPRINT",FACE,{"disambiguationData":[TD([[makeQuery(id+"F16.imprint","IMPRINT",EDGE,{"derivedFrom":subQ8}),1.0]])]});}
            var Q2;
            {var subQ0=sQuery(id+"F16.wireOp",EDGE,"E90");Q2=makeQuery(id+"F16.imprint","IMPRINT",FACE,{"disambiguationData":[TD([[makeQuery(id+"F16.imprint","IMPRINT",EDGE,{"derivedFrom":subQ0}),-1.0]])]});}
            var Q3;
            {var subQ0=sQuery(id+"F16.wireOp",EDGE,"E97.MirrorCS");Q3=makeQuery(id+"F16.imprint","IMPRINT",FACE,{"disambiguationData":[TD([[makeQuery(id+"F16.imprint","IMPRINT",EDGE,{"derivedFrom":subQ0}),1.0]])]});}
            var Q4;
            Q4=makeQuery(id+"F2.opExtrude","CAP_FACE",FACE,{"disambiguationData":[OSD([sQuery(id+"F0.wireOp",EDGE,"E12"),sQuery(id+"F0.wireOp",EDGE,"E13"),sQuery(id+"F0.wireOp",EDGE,"E14"),sQuery(id+"F0.wireOp",EDGE,"E15"),sQuery(id+"F0.wireOp",EDGE,"E17.filletArc"),sQuery(id+"F0.wireOp",EDGE,"E18.filletArc"),sQuery(id+"F0.wireOp",EDGE,"E19.filletArc"),sQuery(id+"F0.wireOp",EDGE,"E20.filletArc"),sQuery(id+"F0.wireOp",EDGE,"E25.0"),sQuery(id+"F0.wireOp",EDGE,"E25.1"),sQuery(id+"F0.wireOp",EDGE,"E25.2"),sQuery(id+"F0.wireOp",EDGE,"E25.3"),sQuery(id+"F0.wireOp",EDGE,"E25.4"),sQuery(id+"F0.wireOp",EDGE,"E25.5"),sQuery(id+"F0.wireOp",EDGE,"E25.6"),sQuery(id+"F0.wireOp",EDGE,"E25.7")])],"isStart":false});
            extrude(context, id + "F17", {"entities" : qUnion([Q0, Q1, Q2, Q3]), "endBound" : BoundingType.UP_TO_SURFACE, "endBoundEntityFace" : qUnion([Q4]), "depth" : 25 * mm});
        }
    });
